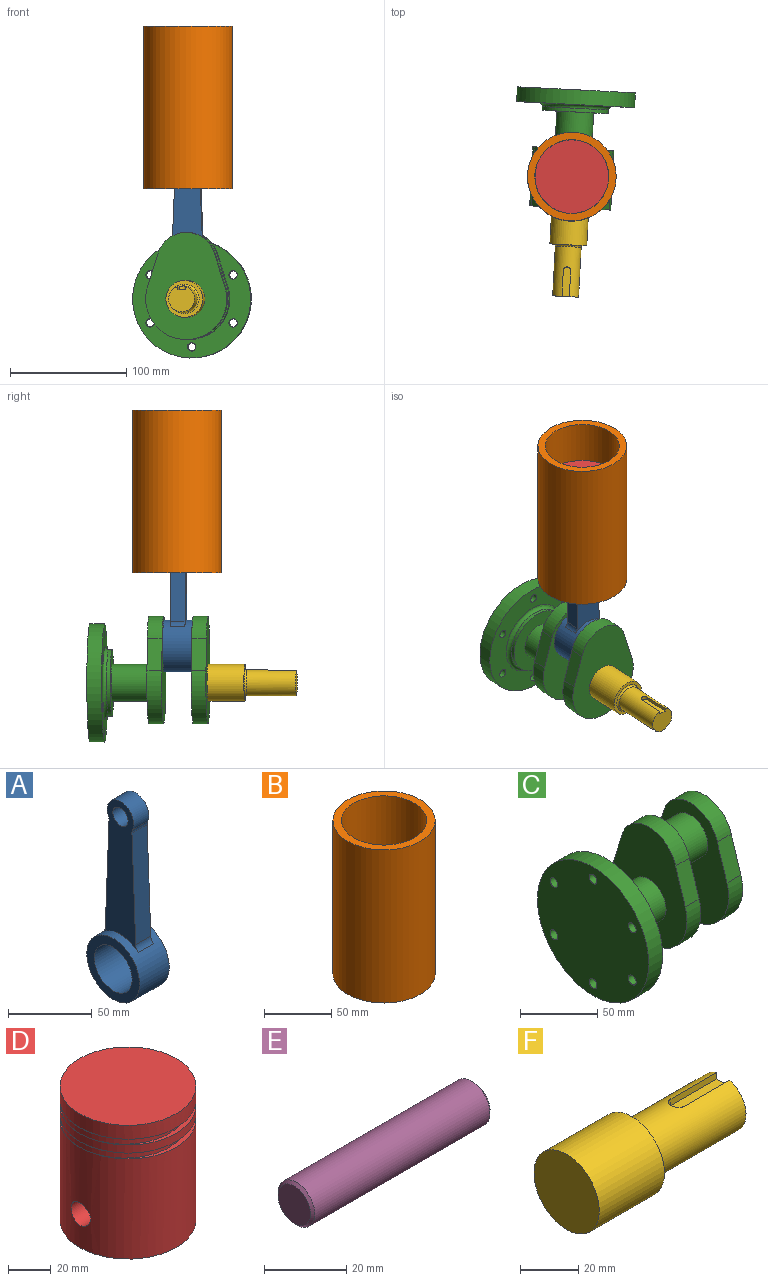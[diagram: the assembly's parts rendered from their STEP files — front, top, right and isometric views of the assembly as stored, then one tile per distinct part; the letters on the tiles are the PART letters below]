
ASSEMBLY  parts=6 mates=5
PART A: 14 faces, bbox 24.9x44.5x141.3 mm
  f0: cylinder r=15.88mm len=31.75mm, axis (-1,0,0), area 2482.9mm2, adj f2,f3
  f1: cylinder r=22.23mm len=44.45mm, axis (-1,0,0), area 3061.2mm2, adj f2,f3,f4,f5,f10,f11
  f2: plane 44.45x44.45mm, normal (1,0,0), area 760.1mm2, adj f0,f1
  f3: plane 44.45x44.45mm, normal (-1,0,0), area 760.1mm2, adj f0,f1
  f4: plane 102.57x29.8mm, normal (1,0,0), area 2012.4mm2, adj f1,f6,f7,f8,f9,f10,f11,f12
  f5: plane 102.57x29.8mm, normal (-1,0,0), area 2012.4mm2, adj f1,f6,f7,f8,f9,f10,f11,f12
  f6: plane 79.73x12.7mm, normal (0,1,0.04), area 1013.4mm2, adj f4,f5,f10,f12
  f7: cylinder r=11.11mm len=22.23mm, axis (-1,0,0), area 560mm2, adj f4,f5,f12,f13
  f8: plane 79.73x12.7mm, normal (0,-1,0.04), area 1013.4mm2, adj f4,f5,f11,f13
  f9: cylinder r=6.35mm len=12.7mm, axis (-1,0,0), area 506.7mm2, adj f4,f5
  f10: cylinder r=6.35mm len=12.7mm, axis (-1,0,0), area 64.2mm2, adj f1,f4,f5,f6
  f11: cylinder r=6.35mm len=12.7mm, axis (-1,0,0), area 64.2mm2, adj f1,f4,f5,f8
  f12: cylinder r=6.35mm len=12.7mm, axis (-1,0,0), area 36.5mm2, adj f4,f5,f6,f7
  f13: cylinder r=6.35mm len=12.7mm, axis (-1,0,0), area 36.5mm2, adj f4,f5,f7,f8
PART B: 4 faces, bbox 76.2x76.2x139.7 mm
  f0: cylinder r=31.75mm len=139.7mm, axis (0,0,-1), area 27868.9mm2, adj f2,f3
  f1: cylinder r=38.1mm len=139.7mm, axis (0,0,-1), area 33442.7mm2, adj f2,f3
  f2: plane 76.2x76.2mm, normal (0,0,1), area 1393.4mm2, adj f0,f1
  f3: plane 76.2x76.2mm, normal (0,0,-1), area 1393.4mm2, adj f0,f1
PART C: 26 faces, bbox 101.6x101.6x108 mm
  f0: cylinder r=50.8mm len=101.6mm, axis (-1,0,0), area 4053.7mm2, adj f1,f2
  f1: plane 101.6x101.6mm, normal (1,0,0), area 4700.3mm2, adj f0,f19,f20,f21,f22,f23,f24,f25
  f2: plane 101.6x101.6mm, normal (-1,0,0), area 7867.3mm2, adj f0,f20,f21,f22,f23,f24,f25
  f3: cylinder r=28.57mm len=57.15mm, axis (-1,0,0), area 570mm2, adj f4,f19
  f4: plane 57.15x57.15mm, normal (1,0,0), area 1773.5mm2, adj f3,f5
  f5: cylinder r=15.88mm len=31.75mm, axis (-1,0,0), area 3166.9mm2, adj f4,f11
  f6: plane 27.84x12.7mm, normal (0,0.95,0.3), area 370.8mm2, adj f7,f9,f10,f11
  f7: cylinder r=25.4mm len=49.16mm, axis (-1,0,0), area 849.5mm2, adj f6,f8,f10,f11
  f8: plane 27.96x12.7mm, normal (0,-0.95,0.3), area 372.3mm2, adj f7,f9,f10,f11
  f9: cylinder r=34.92mm len=69.85mm, axis (-1,0,0), area 1657.4mm2, adj f6,f8,f10,f11
  f10: plane 92.08x69.85mm, normal (1,0,0), area 4138.7mm2, adj f6,f7,f8,f9,f12
  f11: plane 92.08x69.85mm, normal (-1,0,0), area 4138.7mm2, adj f5,f6,f7,f8,f9
  f12: cylinder r=15.88mm len=31.75mm, axis (-1,0,0), area 2533.5mm2, adj f10,f17
  f13: plane 27.84x12.7mm, normal (0,0.95,0.3), area 370.8mm2, adj f14,f16,f17,f18
  f14: cylinder r=34.92mm len=69.85mm, axis (1,0,0), area 1657.4mm2, adj f13,f15,f17,f18
  f15: plane 27.96x12.7mm, normal (0,-0.95,0.3), area 372.3mm2, adj f14,f16,f17,f18
  f16: cylinder r=25.4mm len=49.16mm, axis (1,0,0), area 849.5mm2, adj f13,f15,f17,f18
  f17: plane 92.08x69.85mm, normal (-1,0,0), area 4138.7mm2, adj f12,f13,f14,f15,f16
  f18: plane 92.08x69.85mm, normal (1,0,0), area 4930.5mm2, adj f13,f14,f15,f16
  f19: torus R=31.75mm, axis (1,0,0), area 931.6mm2, adj f1,f3
  f20: cylinder r=3.57mm len=12.7mm, axis (-1,0,0), area 284.8mm2, adj f1,f2
  f21: cylinder r=3.57mm len=12.7mm, axis (-1,0,0), area 284.8mm2, adj f1,f2
  f22: cylinder r=3.57mm len=12.7mm, axis (-1,0,0), area 284.8mm2, adj f1,f2
  f23: cylinder r=3.57mm len=12.7mm, axis (-1,0,0), area 284.8mm2, adj f1,f2
  f24: cylinder r=3.57mm len=12.7mm, axis (-1,0,0), area 284.8mm2, adj f1,f2
  f25: cylinder r=3.57mm len=12.7mm, axis (-1,0,0), area 284.8mm2, adj f1,f2
PART D: 22 faces, bbox 63.2x63.2x76.2 mm
  f0: cylinder r=31.62mm len=63.25mm, axis (0,0,-1), area 11091.3mm2, adj f8,f11,f16,f19
  f1: cone r=28.57mm half-angle=5deg, axis (0,0,-1), area 7106.5mm2, adj f11,f13,f20,f21
  f2: cylinder r=31.62mm len=63.25mm, axis (0,0,-1), area 918.5mm2, adj f3,f9
  f3: plane 63.25x63.25mm, normal (0,0,1), area 422.9mm2, adj f2,f5
  f4: plane 63.25x63.25mm, normal (0,0,-1), area 422.9mm2, adj f5,f7
  f5: cylinder r=29.42mm len=58.84mm, axis (0,0,-1), area 610.3mm2, adj f3,f4
  f6: plane 63.25x63.25mm, normal (0,0,1), area 3141.6mm2, adj f7
  f7: cylinder r=31.62mm len=63.25mm, axis (0,0,-1), area 1564.5mm2, adj f4,f6
  f8: plane 63.25x63.25mm, normal (0,0,1), area 422.9mm2, adj f0,f10
  f9: plane 63.25x63.25mm, normal (0,0,-1), area 422.9mm2, adj f2,f10
  f10: cylinder r=29.42mm len=58.84mm, axis (0,0,-1), area 610.3mm2, adj f8,f9
  f11: plane 63.25x63.25mm, normal (0,0,-1), area 576.4mm2, adj f0,f1
  f12: plane 28.35x28.35mm, normal (0,0,-1), area 631.2mm2, adj f13
  f13: torus R=14.18mm, axis (0,0,1), area 1809.6mm2, adj f1,f12
  f14: plane 25.4x25.4mm, normal (-1,0,0), area 380mm2, adj f15,f16
  f15: cylinder r=12.7mm len=25.4mm, axis (-1,0,0), area 1090.8mm2, adj f14,f21
  f16: cylinder r=6.35mm len=24.29mm, axis (-1,0,0), area 956.3mm2, adj f0,f14
  f17: cylinder r=12.7mm len=25.4mm, axis (1,0,0), area 706mm2, adj f18,f20
  f18: plane 25.4x25.4mm, normal (1,0,0), area 380mm2, adj f17,f19
  f19: cylinder r=6.35mm len=19.91mm, axis (1,0,0), area 781.4mm2, adj f0,f18
  f20: bspline ~35.99x31.76mm, area 569mm2, adj f1,f17
  f21: bspline ~36x31.77mm, area 568.7mm2, adj f1,f15
PART E: 5 faces, bbox 61.9x12.7x12.7 mm
  f0: cylinder r=6.35mm len=60.38mm, axis (-1,0,0), area 2408.9mm2, adj f3,f4
  f1: plane 11.18x11.18mm, normal (1,0,0), area 98.1mm2, adj f4
  f2: plane 11.18x11.18mm, normal (-1,0,0), area 98.1mm2, adj f3
  f3: cone r=6.35mm half-angle=45deg, axis (1,0,0), area 40.4mm2, adj f0,f2
  f4: cone r=5.59mm half-angle=45deg, axis (-1,0,0), area 40.4mm2, adj f0,f1
PART F: 10 faces, bbox 76.2x31.8x31.8 mm
  f0: cylinder r=11.11mm len=42.86mm, axis (-1,0,0), area 2833.6mm2, adj f4,f6,f7,f8,f9
  f1: cylinder r=15.88mm len=31.75mm, axis (1,0,0), area 3166.9mm2, adj f2,f3
  f2: plane 31.75x31.75mm, normal (-1,0,0), area 791.7mm2, adj f1
  f3: plane 31.75x31.75mm, normal (1,0,0), area 285mm2, adj f1,f9
  f4: plane 22.23x21.76mm, normal (1,0,0), area 368.8mm2, adj f0,f5,f6,f7
  f5: plane 25.4x6.35mm, normal (0,0,1), area 157mm2, adj f4,f6,f7,f8
  f6: plane 22.23x2.71mm, normal (0,-1,0), area 60.3mm2, adj f0,f4,f5,f8
  f7: plane 22.23x2.71mm, normal (0,1,0), area 60.3mm2, adj f0,f4,f5,f8
  f8: cylinder r=3.17mm len=6.35mm, axis (0,0,-1), area 29.4mm2, adj f0,f5,f6,f7
  f9: torus R=12.7mm, axis (-1,0,0), area 183.1mm2, adj f0,f3
PLACE A rot(axis=(0,0,-1),93deg) t=(14.68,24.49,-93.56)mm
PLACE B rot(axis=(0,0,-1),93deg) t=(14.74,25.66,-30.48)mm
PLACE C rot(axis=(0,0,-1),93deg) t=(18.62,100.59,-125.31)mm
PLACE D rot(axis=(0,0,-1),93deg) t=(14.86,27.85,-4.69)mm
PLACE E rot(axis=(0,0,-1),93deg) t=(14.82,27.22,14.39)mm
PLACE F rot(axis=(0,0,-1),93deg) t=(18.62,100.59,-125.31)mm
MATE slider B.f0 <-> D.f0  axis (0,0,-1) through (14.74,25.66,39.37)mm
MATE revolute E.f0 <-> D.f16  axis (-0.05,-1,0) through (16.38,57.37,14.39)mm
MATE fastened F.f0 <-> C.f0  axis (0.05,1,0) through (13.37,-0.88,-125.31)mm
MATE slider E.f0 <-> A.f7  axis (0.05,1,0) through (14.82,27.22,14.39)mm
MATE revolute A.f0 <-> C.f7  axis (0.05,1,0) through (14.68,24.49,-93.56)mm
